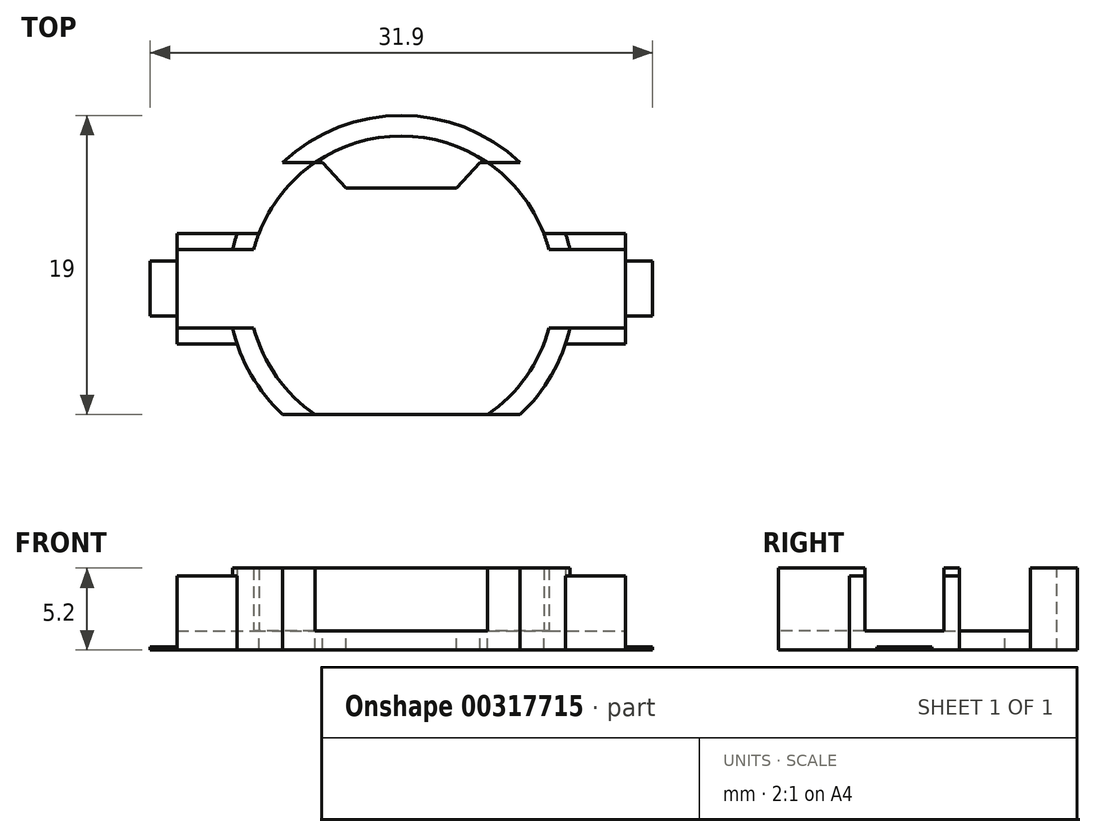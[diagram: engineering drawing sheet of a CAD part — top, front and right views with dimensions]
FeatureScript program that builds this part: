
annotation { "Feature Type Name" : "Feature", "Feature Type Description" : "" }
export const myFeature = defineFeature(function(context is Context, id is Id, definition is map)
    precondition{}
    {
        {
            var Q0;
            Q0=qCreatedBy(makeId("Top.planeOp"),FACE);
            var sketch = newSketch(context, id + "F0", { "sketchPlane" : qUnion([Q0])});
            skCircle(sketch, "E0", {"center": v(0, 0) * mm, "radius": 11 * mm});
            skLineSegment(sketch, "E1", {"start": v(-7.55, 8) * mm, "end": v(7.55, 8) * mm});
            skLineSegment(sketch, "E2", {"start": v(-7.55, -8) * mm, "end": v(7.55, -8) * mm});
            skCircle(sketch, "E3.0", {"center": v(0, 0) * mm, "radius": 9.7 * mm});
            skLineSegment(sketch, "E4.bottom", {"start": v(-14.25, 3.5) * mm, "end": v(14.25, 3.5) * mm});
            skLineSegment(sketch, "E4.top", {"start": v(-14.25, -3.5) * mm, "end": v(14.25, -3.5) * mm});
            skLineSegment(sketch, "E4.left", {"start": v(-14.25, 3.5) * mm, "end": v(-14.25, -3.5) * mm});
            skLineSegment(sketch, "E4.right", {"start": v(14.25, 3.5) * mm, "end": v(14.25, -3.5) * mm});
            skPoint(sketch, "E5", {"position": v(-14.25, 0) * mm});
            skPoint(sketch, "E6", {"position": v(0, 3.5) * mm});
            skPoint(sketch, "E7", {"position": v(16.05, 0) * mm});
            skLineSegment(sketch, "E8", {"start": v(-5, 8) * mm, "end": v(-3.5, 6.4) * mm});
            skLineSegment(sketch, "E9", {"start": v(-3.5, 6.4) * mm, "end": v(3.5, 6.4) * mm});
            skLineSegment(sketch, "E10", {"start": v(3.5, 6.4) * mm, "end": v(5, 8) * mm});
            skPoint(sketch, "E11", {"position": v(0, 6.4) * mm});
            skLineSegment(sketch, "E12", {"start": v(-5, 8) * mm, "end": v(5, 8) * mm});
            skPoint(sketch, "E13", {"position": v(0, 8) * mm});
            skLineSegment(sketch, "E14", {"start": v(14.25, 2.5) * mm, "end": v(9.37, 2.5) * mm});
            skLineSegment(sketch, "E15", {"start": v(9.37, -2.5) * mm, "end": v(14.25, -2.5) * mm});
            skLineSegment(sketch, "E16.MirrorCS", {"start": v(-9.37, -2.5) * mm, "end": v(-14.25, -2.5) * mm});
            skLineSegment(sketch, "E17.MirrorCS", {"start": v(-14.25, 2.5) * mm, "end": v(-9.37, 2.5) * mm});
            skSolve(sketch);
        }
        {
            var Q0;
            {var subQ0=sQuery(id+"F0.wireOp",EDGE,"E4.bottom");var subQ1=sQuery(id+"F0.wireOp",EDGE,"E0");var subQ2=makeQuery(id+"F0.imprint","INTERSECT",VERTEX,{"disambiguationData":[OD(1.0)],"derivedFrom":[subQ1,subQ0]});Q0=makeQuery(id+"F0.imprint","IMPRINT",FACE,{"disambiguationData":[TD([[makeQuery(id+"F0.imprint","IMPRINT",EDGE,{"disambiguationData":[TD([[subQ2,-1.0]])],"derivedFrom":subQ1}),-1.0]])]});}
            var Q1;
            {var subQ0=sQuery(id+"F0.wireOp",EDGE,"eaab76ed-f881-47aa-8fd5-868684c00cd50.MirrorCS");Q1=makeQuery(id+"F0.imprint","IMPRINT",FACE,{"disambiguationData":[TD([[makeQuery(id+"F0.imprint","IMPRINT",EDGE,{"derivedFrom":subQ0}),1.0]])]});}
            var Q2;
            {var subQ0=sQuery(id+"F0.wireOp",EDGE,"E4.top");var subQ1=sQuery(id+"F0.wireOp",EDGE,"E0");var subQ2=makeQuery(id+"F0.imprint","INTERSECT",VERTEX,{"disambiguationData":[OD(0.0)],"derivedFrom":[subQ1,subQ0]});Q2=makeQuery(id+"F0.imprint","IMPRINT",FACE,{"disambiguationData":[TD([[makeQuery(id+"F0.imprint","IMPRINT",EDGE,{"disambiguationData":[TD([[subQ2,1.0]])],"derivedFrom":subQ1}),-1.0]])]});}
            var Q3;
            {var subQ0=sQuery(id+"F0.wireOp",EDGE,"E4.top");var subQ1=sQuery(id+"F0.wireOp",EDGE,"E0");var subQ2=makeQuery(id+"F0.imprint","INTERSECT",VERTEX,{"disambiguationData":[OD(0.0)],"derivedFrom":[subQ1,subQ0]});Q3=makeQuery(id+"F0.imprint","IMPRINT",FACE,{"disambiguationData":[TD([[makeQuery(id+"F0.imprint","IMPRINT",EDGE,{"disambiguationData":[TD([[subQ2,1.0]])],"derivedFrom":subQ1}),1.0]])]});}
            var Q4;
            {var subQ0=sQuery(id+"F0.wireOp",EDGE,"E4.bottom");var subQ1=sQuery(id+"F0.wireOp",EDGE,"E0");var subQ2=makeQuery(id+"F0.imprint","INTERSECT",VERTEX,{"disambiguationData":[OD(1.0)],"derivedFrom":[subQ1,subQ0]});Q4=makeQuery(id+"F0.imprint","IMPRINT",FACE,{"disambiguationData":[TD([[makeQuery(id+"F0.imprint","IMPRINT",EDGE,{"disambiguationData":[TD([[subQ2,-1.0]])],"derivedFrom":subQ1}),1.0]])]});}
            var Q5;
            {var subQ0=sQuery(id+"F0.wireOp",EDGE,"E17.MirrorCS");var subQ1=sQuery(id+"F0.wireOp",EDGE,"E0");var subQ2=makeQuery(id+"F0.imprint","INTERSECT",VERTEX,{"derivedFrom":[subQ1,subQ0]});Q5=makeQuery(id+"F0.imprint","IMPRINT",FACE,{"disambiguationData":[TD([[makeQuery(id+"F0.imprint","IMPRINT",EDGE,{"disambiguationData":[TD([[subQ2,-1.0]])],"derivedFrom":subQ1}),1.0]])]});}
            var Q6;
            {var subQ9=sQuery(id+"F0.wireOp",EDGE,"E8");Q6=makeQuery(id+"F0.imprint","IMPRINT",FACE,{"disambiguationData":[TD([[makeQuery(id+"F0.imprint","IMPRINT",EDGE,{"derivedFrom":subQ9}),-1.0]])]});}
            var Q7;
            {var subQ0=sQuery(id+"F0.wireOp",EDGE,"E3.0");var subQ7=makeQuery(id+"F0.imprint","INTERSECT",VERTEX,{"derivedFrom":[subQ0,sQuery(id+"F0.wireOp",EDGE,"E14")]});Q7=makeQuery(id+"F0.imprint","IMPRINT",FACE,{"disambiguationData":[TD([[makeQuery(id+"F0.imprint","IMPRINT",EDGE,{"disambiguationData":[TD([[subQ7,-1.0]])],"derivedFrom":subQ0}),1.0]])]});}
            var Q8;
            {var subQ0=sQuery(id+"F0.wireOp",EDGE,"E1");var subQ1=sQuery(id+"F0.wireOp",EDGE,"E0");var subQ2=makeQuery(id+"F0.imprint","INTERSECT",VERTEX,{"disambiguationData":[OD(0.0)],"derivedFrom":[subQ1,subQ0]});Q8=makeQuery(id+"F0.imprint","IMPRINT",FACE,{"disambiguationData":[TD([[makeQuery(id+"F0.imprint","IMPRINT",EDGE,{"disambiguationData":[TD([[subQ2,-1.0]])],"derivedFrom":subQ1}),1.0]])]});}
            var Q9;
            {var subQ0=sQuery(id+"F0.wireOp",EDGE,"E1");var subQ1=sQuery(id+"F0.wireOp",EDGE,"E0");var subQ2=makeQuery(id+"F0.imprint","INTERSECT",VERTEX,{"disambiguationData":[OD(1.0)],"derivedFrom":[subQ1,subQ0]});Q9=makeQuery(id+"F0.imprint","IMPRINT",FACE,{"disambiguationData":[TD([[makeQuery(id+"F0.imprint","IMPRINT",EDGE,{"disambiguationData":[TD([[subQ2,1.0]])],"derivedFrom":subQ1}),1.0]])]});}
            var Q10;
            {var subQ0=sQuery(id+"F0.wireOp",EDGE,"E4.bottom");var subQ1=sQuery(id+"F0.wireOp",EDGE,"E0");var subQ2=makeQuery(id+"F0.imprint","INTERSECT",VERTEX,{"disambiguationData":[OD(0.0)],"derivedFrom":[subQ1,subQ0]});Q10=makeQuery(id+"F0.imprint","IMPRINT",FACE,{"disambiguationData":[TD([[makeQuery(id+"F0.imprint","IMPRINT",EDGE,{"disambiguationData":[TD([[subQ2,1.0]])],"derivedFrom":subQ1}),-1.0]])]});}
            var Q11;
            {var subQ0=sQuery(id+"F0.wireOp",EDGE,"pLYkgnK4-1g5J-ED7h-OX47-ZcyXQC5KojmQ.left");Q11=makeQuery(id+"F0.imprint","IMPRINT",FACE,{"disambiguationData":[TD([[makeQuery(id+"F0.imprint","IMPRINT",EDGE,{"derivedFrom":subQ0}),-1.0]])]});}
            var Q12;
            {var subQ0=sQuery(id+"F0.wireOp",EDGE,"E4.top");var subQ1=sQuery(id+"F0.wireOp",EDGE,"E0");var subQ2=makeQuery(id+"F0.imprint","INTERSECT",VERTEX,{"disambiguationData":[OD(1.0)],"derivedFrom":[subQ1,subQ0]});Q12=makeQuery(id+"F0.imprint","IMPRINT",FACE,{"disambiguationData":[TD([[makeQuery(id+"F0.imprint","IMPRINT",EDGE,{"disambiguationData":[TD([[subQ2,-1.0]])],"derivedFrom":subQ1}),-1.0]])]});}
            var Q13;
            {var subQ0=sQuery(id+"F0.wireOp",EDGE,"E4.top");var subQ1=sQuery(id+"F0.wireOp",EDGE,"E0");var subQ2=makeQuery(id+"F0.imprint","INTERSECT",VERTEX,{"disambiguationData":[OD(1.0)],"derivedFrom":[subQ1,subQ0]});Q13=makeQuery(id+"F0.imprint","IMPRINT",FACE,{"disambiguationData":[TD([[makeQuery(id+"F0.imprint","IMPRINT",EDGE,{"disambiguationData":[TD([[subQ2,-1.0]])],"derivedFrom":subQ1}),1.0]])]});}
            var Q14;
            {var subQ0=sQuery(id+"F0.wireOp",EDGE,"E14");var subQ1=sQuery(id+"F0.wireOp",EDGE,"E0");var subQ2=makeQuery(id+"F0.imprint","INTERSECT",VERTEX,{"derivedFrom":[subQ1,subQ0]});Q14=makeQuery(id+"F0.imprint","IMPRINT",FACE,{"disambiguationData":[TD([[makeQuery(id+"F0.imprint","IMPRINT",EDGE,{"disambiguationData":[TD([[subQ2,1.0]])],"derivedFrom":subQ1}),1.0]])]});}
            var Q15;
            {var subQ0=sQuery(id+"F0.wireOp",EDGE,"E4.bottom");var subQ1=sQuery(id+"F0.wireOp",EDGE,"E0");var subQ2=makeQuery(id+"F0.imprint","INTERSECT",VERTEX,{"disambiguationData":[OD(0.0)],"derivedFrom":[subQ1,subQ0]});Q15=makeQuery(id+"F0.imprint","IMPRINT",FACE,{"disambiguationData":[TD([[makeQuery(id+"F0.imprint","IMPRINT",EDGE,{"disambiguationData":[TD([[subQ2,1.0]])],"derivedFrom":subQ1}),1.0]])]});}
            var Q16;
            {var subQ0=sQuery(id+"F0.wireOp",EDGE,"E2");var subQ1=sQuery(id+"F0.wireOp",EDGE,"E0");var subQ2=makeQuery(id+"F0.imprint","INTERSECT",VERTEX,{"disambiguationData":[OD(1.0)],"derivedFrom":[subQ1,subQ0]});Q16=makeQuery(id+"F0.imprint","IMPRINT",FACE,{"disambiguationData":[TD([[makeQuery(id+"F0.imprint","IMPRINT",EDGE,{"disambiguationData":[TD([[subQ2,-1.0]])],"derivedFrom":subQ1}),1.0]])]});}
            var Q17;
            {var subQ0=sQuery(id+"F0.wireOp",EDGE,"E3.0");var subQ1=sQuery(id+"F0.wireOp",EDGE,"E2");var subQ2=makeQuery(id+"F0.imprint","INTERSECT",VERTEX,{"disambiguationData":[OD(0.0)],"derivedFrom":[subQ1,subQ0]});Q17=makeQuery(id+"F0.imprint","IMPRINT",FACE,{"disambiguationData":[TD([[makeQuery(id+"F0.imprint","IMPRINT",EDGE,{"disambiguationData":[TD([[subQ2,-1.0]])],"derivedFrom":subQ1}),1.0]])]});}
            var Q18;
            {var subQ0=sQuery(id+"F0.wireOp",EDGE,"E2");var subQ1=sQuery(id+"F0.wireOp",EDGE,"E0");var subQ2=makeQuery(id+"F0.imprint","INTERSECT",VERTEX,{"disambiguationData":[OD(0.0)],"derivedFrom":[subQ1,subQ0]});Q18=makeQuery(id+"F0.imprint","IMPRINT",FACE,{"disambiguationData":[TD([[makeQuery(id+"F0.imprint","IMPRINT",EDGE,{"disambiguationData":[TD([[subQ2,1.0]])],"derivedFrom":subQ1}),1.0]])]});}
            var Q19;
            {var subQ0=sQuery(id+"F0.wireOp",EDGE,"E17.MirrorCS");var subQ1=sQuery(id+"F0.wireOp",EDGE,"E0");var subQ2=makeQuery(id+"F0.imprint","INTERSECT",VERTEX,{"derivedFrom":[subQ1,subQ0]});Q19=makeQuery(id+"F0.imprint","IMPRINT",FACE,{"disambiguationData":[TD([[makeQuery(id+"F0.imprint","IMPRINT",EDGE,{"disambiguationData":[TD([[subQ2,-1.0]])],"derivedFrom":subQ1}),-1.0]])]});}
            var Q20;
            {var subQ0=sQuery(id+"F0.wireOp",EDGE,"E14");var subQ1=sQuery(id+"F0.wireOp",EDGE,"E0");var subQ2=makeQuery(id+"F0.imprint","INTERSECT",VERTEX,{"derivedFrom":[subQ1,subQ0]});Q20=makeQuery(id+"F0.imprint","IMPRINT",FACE,{"disambiguationData":[TD([[makeQuery(id+"F0.imprint","IMPRINT",EDGE,{"disambiguationData":[TD([[subQ2,1.0]])],"derivedFrom":subQ1}),-1.0]])]});}
            extrude(context, id + "F1", {"entities" : qUnion([Q0, Q1, Q2, Q3, Q4, Q5, Q6, Q7, Q8, Q9, Q10, Q11, Q12, Q13, Q14, Q15, Q16, Q17, Q18, Q19, Q20]), "oppositeDirection" : true, "depth" : 1.2 * mm});
        }
        {
            var Q0;
            {var subQ0=sQuery(id+"F0.wireOp",EDGE,"E1");var subQ1=sQuery(id+"F0.wireOp",EDGE,"E0");var subQ2=makeQuery(id+"F0.imprint","INTERSECT",VERTEX,{"disambiguationData":[OD(0.0)],"derivedFrom":[subQ1,subQ0]});Q0=makeQuery(id+"F0.imprint","IMPRINT",FACE,{"disambiguationData":[TD([[makeQuery(id+"F0.imprint","IMPRINT",EDGE,{"disambiguationData":[TD([[subQ2,-1.0]])],"derivedFrom":subQ1}),1.0]])]});}
            var Q1;
            {var subQ0=sQuery(id+"F0.wireOp",EDGE,"E4.bottom");var subQ1=sQuery(id+"F0.wireOp",EDGE,"E0");var subQ2=makeQuery(id+"F0.imprint","INTERSECT",VERTEX,{"disambiguationData":[OD(1.0)],"derivedFrom":[subQ1,subQ0]});Q1=makeQuery(id+"F0.imprint","IMPRINT",FACE,{"disambiguationData":[TD([[makeQuery(id+"F0.imprint","IMPRINT",EDGE,{"disambiguationData":[TD([[subQ2,-1.0]])],"derivedFrom":subQ1}),1.0]])]});}
            var Q2;
            {var subQ0=sQuery(id+"F0.wireOp",EDGE,"E4.top");var subQ1=sQuery(id+"F0.wireOp",EDGE,"E0");var subQ2=makeQuery(id+"F0.imprint","INTERSECT",VERTEX,{"disambiguationData":[OD(0.0)],"derivedFrom":[subQ1,subQ0]});Q2=makeQuery(id+"F0.imprint","IMPRINT",FACE,{"disambiguationData":[TD([[makeQuery(id+"F0.imprint","IMPRINT",EDGE,{"disambiguationData":[TD([[subQ2,1.0]])],"derivedFrom":subQ1}),1.0]])]});}
            var Q3;
            {var subQ0=sQuery(id+"F0.wireOp",EDGE,"E2");var subQ1=sQuery(id+"F0.wireOp",EDGE,"E0");var subQ2=makeQuery(id+"F0.imprint","INTERSECT",VERTEX,{"disambiguationData":[OD(0.0)],"derivedFrom":[subQ1,subQ0]});Q3=makeQuery(id+"F0.imprint","IMPRINT",FACE,{"disambiguationData":[TD([[makeQuery(id+"F0.imprint","IMPRINT",EDGE,{"disambiguationData":[TD([[subQ2,1.0]])],"derivedFrom":subQ1}),1.0]])]});}
            var Q4;
            {var subQ0=sQuery(id+"F0.wireOp",EDGE,"E2");var subQ1=sQuery(id+"F0.wireOp",EDGE,"E0");var subQ2=makeQuery(id+"F0.imprint","INTERSECT",VERTEX,{"disambiguationData":[OD(1.0)],"derivedFrom":[subQ1,subQ0]});Q4=makeQuery(id+"F0.imprint","IMPRINT",FACE,{"disambiguationData":[TD([[makeQuery(id+"F0.imprint","IMPRINT",EDGE,{"disambiguationData":[TD([[subQ2,-1.0]])],"derivedFrom":subQ1}),1.0]])]});}
            var Q5;
            {var subQ0=sQuery(id+"F0.wireOp",EDGE,"E4.top");var subQ1=sQuery(id+"F0.wireOp",EDGE,"E0");var subQ2=makeQuery(id+"F0.imprint","INTERSECT",VERTEX,{"disambiguationData":[OD(1.0)],"derivedFrom":[subQ1,subQ0]});Q5=makeQuery(id+"F0.imprint","IMPRINT",FACE,{"disambiguationData":[TD([[makeQuery(id+"F0.imprint","IMPRINT",EDGE,{"disambiguationData":[TD([[subQ2,-1.0]])],"derivedFrom":subQ1}),1.0]])]});}
            var Q6;
            {var subQ0=sQuery(id+"F0.wireOp",EDGE,"E1");var subQ1=sQuery(id+"F0.wireOp",EDGE,"E0");var subQ2=makeQuery(id+"F0.imprint","INTERSECT",VERTEX,{"disambiguationData":[OD(1.0)],"derivedFrom":[subQ1,subQ0]});Q6=makeQuery(id+"F0.imprint","IMPRINT",FACE,{"disambiguationData":[TD([[makeQuery(id+"F0.imprint","IMPRINT",EDGE,{"disambiguationData":[TD([[subQ2,1.0]])],"derivedFrom":subQ1}),1.0]])]});}
            var Q7;
            {var subQ0=sQuery(id+"F0.wireOp",EDGE,"E4.bottom");var subQ1=sQuery(id+"F0.wireOp",EDGE,"E0");var subQ2=makeQuery(id+"F0.imprint","INTERSECT",VERTEX,{"disambiguationData":[OD(0.0)],"derivedFrom":[subQ1,subQ0]});Q7=makeQuery(id+"F0.imprint","IMPRINT",FACE,{"disambiguationData":[TD([[makeQuery(id+"F0.imprint","IMPRINT",EDGE,{"disambiguationData":[TD([[subQ2,1.0]])],"derivedFrom":subQ1}),1.0]])]});}
            extrude(context, id + "F2", {"entities" : qUnion([Q0, Q1, Q2, Q3, Q4, Q5, Q6, Q7]), "operationType" : NewBodyOperationType.ADD, "depth" : 4 * mm});
        }
        {
            var Q0;
            {var subQ0=sQuery(id+"F0.wireOp",EDGE,"E4.bottom");var subQ1=sQuery(id+"F0.wireOp",EDGE,"E0");var subQ2=makeQuery(id+"F0.imprint","INTERSECT",VERTEX,{"disambiguationData":[OD(1.0)],"derivedFrom":[subQ1,subQ0]});Q0=makeQuery(id+"F0.imprint","IMPRINT",FACE,{"disambiguationData":[TD([[makeQuery(id+"F0.imprint","IMPRINT",EDGE,{"disambiguationData":[TD([[subQ2,-1.0]])],"derivedFrom":subQ1}),-1.0]])]});}
            var Q1;
            {var subQ0=sQuery(id+"F0.wireOp",EDGE,"E4.top");var subQ1=sQuery(id+"F0.wireOp",EDGE,"E0");var subQ2=makeQuery(id+"F0.imprint","INTERSECT",VERTEX,{"disambiguationData":[OD(0.0)],"derivedFrom":[subQ1,subQ0]});Q1=makeQuery(id+"F0.imprint","IMPRINT",FACE,{"disambiguationData":[TD([[makeQuery(id+"F0.imprint","IMPRINT",EDGE,{"disambiguationData":[TD([[subQ2,1.0]])],"derivedFrom":subQ1}),-1.0]])]});}
            var Q2;
            {var subQ0=sQuery(id+"F0.wireOp",EDGE,"E4.top");var subQ1=sQuery(id+"F0.wireOp",EDGE,"E0");var subQ2=makeQuery(id+"F0.imprint","INTERSECT",VERTEX,{"disambiguationData":[OD(1.0)],"derivedFrom":[subQ1,subQ0]});Q2=makeQuery(id+"F0.imprint","IMPRINT",FACE,{"disambiguationData":[TD([[makeQuery(id+"F0.imprint","IMPRINT",EDGE,{"disambiguationData":[TD([[subQ2,-1.0]])],"derivedFrom":subQ1}),-1.0]])]});}
            var Q3;
            {var subQ0=sQuery(id+"F0.wireOp",EDGE,"E4.bottom");var subQ1=sQuery(id+"F0.wireOp",EDGE,"E0");var subQ2=makeQuery(id+"F0.imprint","INTERSECT",VERTEX,{"disambiguationData":[OD(0.0)],"derivedFrom":[subQ1,subQ0]});Q3=makeQuery(id+"F0.imprint","IMPRINT",FACE,{"disambiguationData":[TD([[makeQuery(id+"F0.imprint","IMPRINT",EDGE,{"disambiguationData":[TD([[subQ2,1.0]])],"derivedFrom":subQ1}),-1.0]])]});}
            extrude(context, id + "F3", {"entities" : qUnion([Q0, Q1, Q2, Q3]), "operationType" : NewBodyOperationType.ADD, "depth" : 3.5 * mm});
        }
        {
            var Q0;
            Q0=makeQuery(id+"F1.opExtrude","CAP_FACE",FACE,{"disambiguationData":[OSD([sQuery(id+"F0.wireOp",EDGE,"E0"),sQuery(id+"F0.wireOp",EDGE,"E1"),sQuery(id+"F0.wireOp",EDGE,"E2"),sQuery(id+"F0.wireOp",EDGE,"E4.bottom"),sQuery(id+"F0.wireOp",EDGE,"E4.top"),sQuery(id+"F0.wireOp",EDGE,"E4.left"),sQuery(id+"F0.wireOp",EDGE,"E4.right"),sQuery(id+"F0.wireOp",EDGE,"E8"),sQuery(id+"F0.wireOp",EDGE,"E9"),sQuery(id+"F0.wireOp",EDGE,"E10"),sQuery(id+"F0.wireOp",EDGE,"E14"),sQuery(id+"F0.wireOp",EDGE,"E15"),sQuery(id+"F0.wireOp",EDGE,"E16.MirrorCS"),sQuery(id+"F0.wireOp",EDGE,"E17.MirrorCS")])],"isStart":false});
            var sketch = newSketch(context, id + "F4", { "sketchPlane" : qUnion([Q0])});
            skLineSegment(sketch, "E18.bottom", {"start": v(-14.25, 1.75) * mm, "end": v(-15.95, 1.75) * mm});
            skLineSegment(sketch, "E18.top", {"start": v(-14.25, -1.75) * mm, "end": v(-15.95, -1.75) * mm});
            skLineSegment(sketch, "E18.left", {"start": v(-14.25, 1.75) * mm, "end": v(-14.25, -1.75) * mm});
            skLineSegment(sketch, "E18.right", {"start": v(-15.95, 1.75) * mm, "end": v(-15.95, -1.75) * mm});
            skPoint(sketch, "E19", {"position": v(-15.95, 0) * mm});
            skLineSegment(sketch, "E20.MirrorCS", {"start": v(14.25, 1.75) * mm, "end": v(15.95, 1.75) * mm});
            skLineSegment(sketch, "E21.MirrorCS", {"start": v(14.25, 1.75) * mm, "end": v(14.25, -1.75) * mm});
            skLineSegment(sketch, "E22.MirrorCS", {"start": v(14.25, -1.75) * mm, "end": v(15.95, -1.75) * mm});
            skLineSegment(sketch, "E23.MirrorCS", {"start": v(15.95, 1.75) * mm, "end": v(15.95, -1.75) * mm});
            skSolve(sketch);
        }
        {
            var Q0;
            Q0=makeQuery(id+"F4.imprint","IMPRINT",FACE,{"disambiguationData":[TD([[makeQuery(id+"F4.imprint","IMPRINT",EDGE,{"derivedFrom":sQuery(id+"F4.wireOp",EDGE,"E18.bottom")}),1.0]])]});
            var Q1;
            Q1=makeQuery(id+"F4.imprint","IMPRINT",FACE,{"disambiguationData":[TD([[makeQuery(id+"F4.imprint","IMPRINT",EDGE,{"derivedFrom":sQuery(id+"F4.wireOp",EDGE,"E20.MirrorCS")}),-1.0]])]});
            extrude(context, id + "F5", {"entities" : qUnion([Q0, Q1]), "operationType" : NewBodyOperationType.ADD, "oppositeDirection" : true, "depth" : 0.2 * mm});
        }
    });
